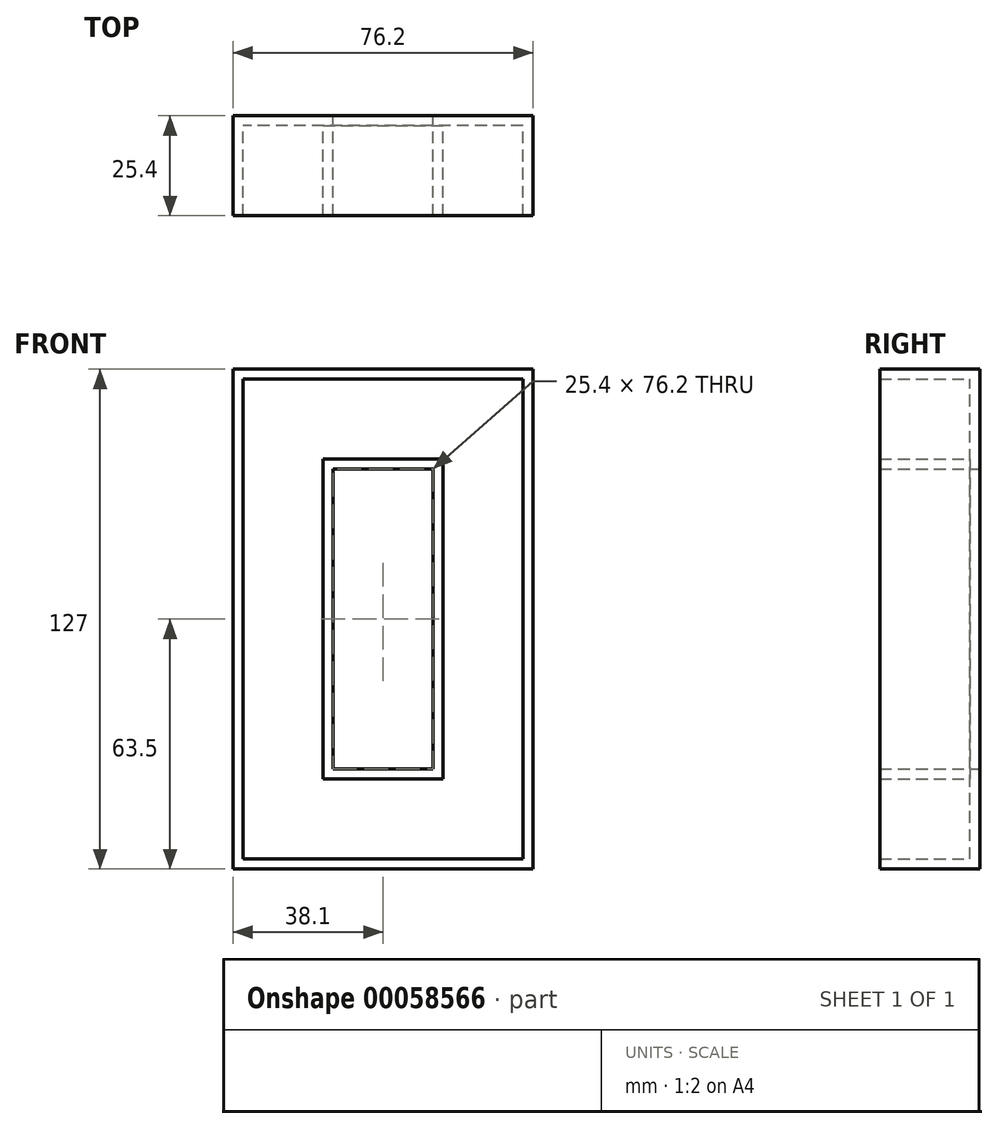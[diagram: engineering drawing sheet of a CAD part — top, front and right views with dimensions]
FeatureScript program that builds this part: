
annotation { "Feature Type Name" : "Feature", "Feature Type Description" : "" }
export const myFeature = defineFeature(function(context is Context, id is Id, definition is map)
    precondition{}
    {
        {
            var Q0;
            Q0=qCreatedBy(makeId("Front.planeOp"),FACE);
            var sketch = newSketch(context, id + "F0", { "sketchPlane" : qUnion([Q0])});
            skLineSegment(sketch, "E0.bottom", {"start": v(0, 0) * mm, "end": v(-76.2, 0) * mm});
            skLineSegment(sketch, "E0.top", {"start": v(0, 127) * mm, "end": v(-76.2, 127) * mm});
            skLineSegment(sketch, "E0.left", {"start": v(0, 0) * mm, "end": v(0, 127) * mm});
            skLineSegment(sketch, "E0.right", {"start": v(-76.2, 0) * mm, "end": v(-76.2, 127) * mm});
            skLineSegment(sketch, "E1.bottom", {"start": v(-50.8, 101.6) * mm, "end": v(-25.4, 101.6) * mm});
            skLineSegment(sketch, "E1.top", {"start": v(-50.8, 25.4) * mm, "end": v(-25.4, 25.4) * mm});
            skLineSegment(sketch, "E1.left", {"start": v(-50.8, 101.6) * mm, "end": v(-50.8, 25.4) * mm});
            skLineSegment(sketch, "E1.right", {"start": v(-25.4, 101.6) * mm, "end": v(-25.4, 25.4) * mm});
            skSolve(sketch);
        }
        {
            var Q0;
            Q0 = qSketchRegion(id + "F0", true);
            extrude(context, id + "F1", {"entities" : qUnion([Q0]), "depth" : 25.4 * mm});
        }
        {
            var Q0;
            Q0=makeQuery(id+"F1.opExtrude","CAP_FACE",FACE,{"disambiguationData":[OSD([sQuery(id+"F0.wireOp",EDGE,"E0.bottom"),sQuery(id+"F0.wireOp",EDGE,"E0.top"),sQuery(id+"F0.wireOp",EDGE,"E0.left"),sQuery(id+"F0.wireOp",EDGE,"E0.right"),sQuery(id+"F0.wireOp",EDGE,"E1.bottom"),sQuery(id+"F0.wireOp",EDGE,"E1.top"),sQuery(id+"F0.wireOp",EDGE,"E1.left"),sQuery(id+"F0.wireOp",EDGE,"E1.right")])],"isStart":false});
            shell(context, id + "F2", {"entities" : qUnion([Q0]), "thickness" : 2.54 * mm});
        }
    });
